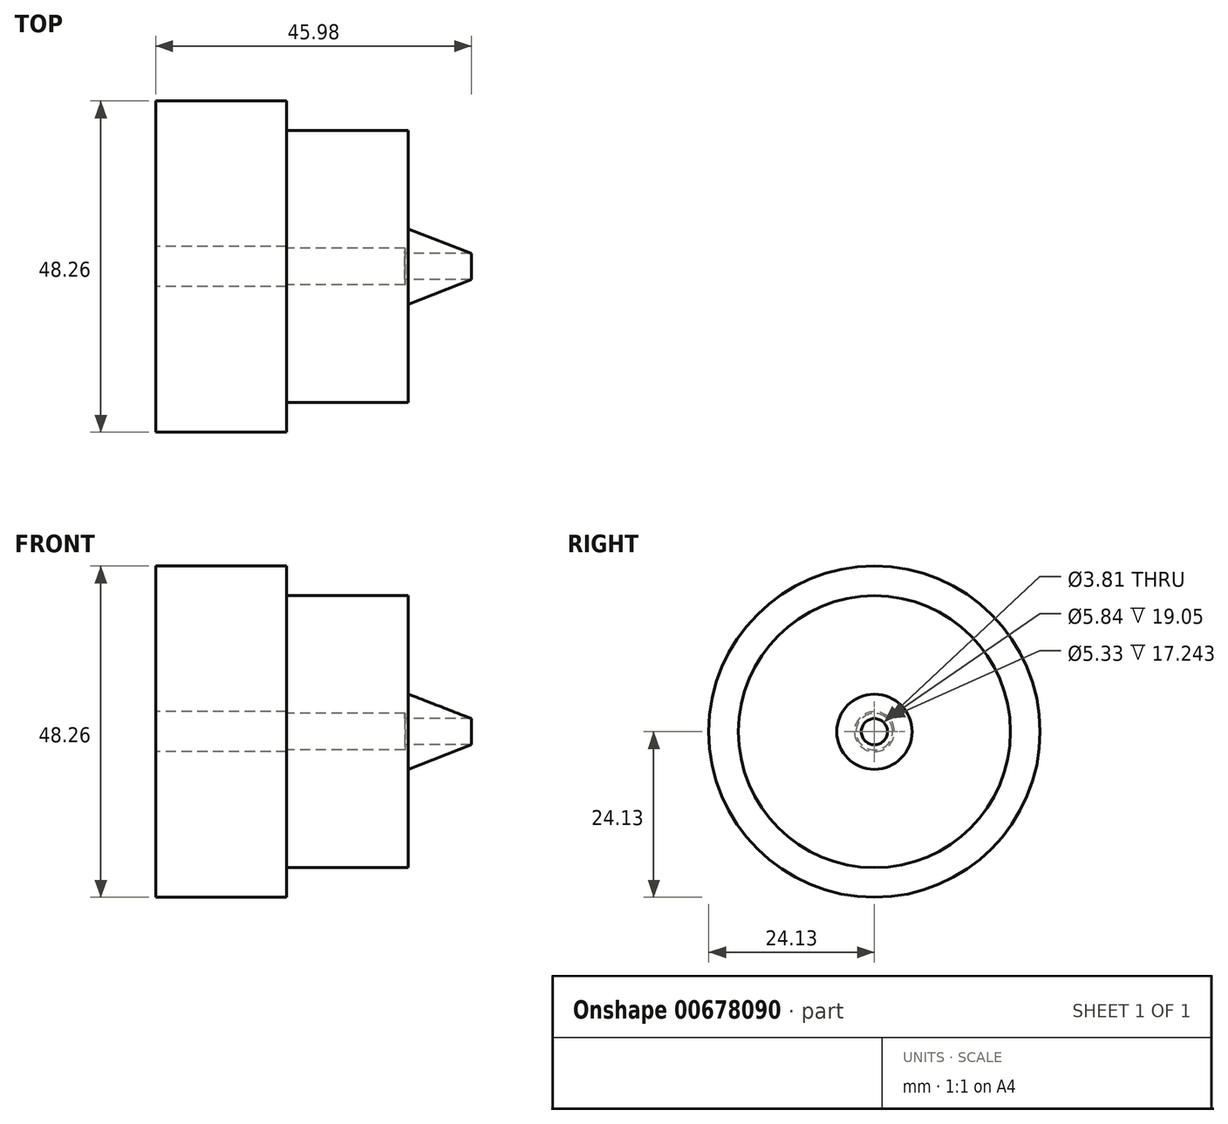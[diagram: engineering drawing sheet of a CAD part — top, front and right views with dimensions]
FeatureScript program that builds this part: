
annotation { "Feature Type Name" : "Feature", "Feature Type Description" : "" }
export const myFeature = defineFeature(function(context is Context, id is Id, definition is map)
    precondition{}
    {
        {
            var Q0;
            Q0=qCreatedBy(makeId("Front.planeOp"),FACE);
            var sketch = newSketch(context, id + "F0", { "sketchPlane" : qUnion([Q0])});
            skLineSegment(sketch, "E0", {"start": v(-45.3, 0) * mm, "end": v(58.06, 0) * mm, "construction": true});
            skLineSegment(sketch, "E1", {"start": v(17.23, 1.9) * mm, "end": v(26.93, 1.9) * mm});
            skLineSegment(sketch, "E2", {"start": v(26.93, 1.9) * mm, "end": v(17.74, 5.48) * mm});
            skLineSegment(sketch, "E3", {"start": v(17.74, 5.48) * mm, "end": v(17.74, 19.81) * mm});
            skLineSegment(sketch, "E4", {"start": v(17.74, 19.81) * mm, "end": v(0, 19.81) * mm});
            skLineSegment(sketch, "E5", {"start": v(0, 19.81) * mm, "end": v(0, 24.13) * mm});
            skLineSegment(sketch, "E6", {"start": v(0, 24.13) * mm, "end": v(-19.05, 24.13) * mm});
            skLineSegment(sketch, "E7", {"start": v(-19.05, 24.13) * mm, "end": v(-19.05, 2.92) * mm});
            skLineSegment(sketch, "E8", {"start": v(-19.05, 2.92) * mm, "end": v(0, 2.92) * mm});
            skLineSegment(sketch, "E9", {"start": v(0, 2.92) * mm, "end": v(0, 2.67) * mm});
            skLineSegment(sketch, "E10", {"start": v(0, 2.67) * mm, "end": v(17.24, 2.67) * mm});
            skLineSegment(sketch, "E11", {"start": v(17.23, 1.9) * mm, "end": v(17.24, 2.67) * mm});
            skSolve(sketch);
        }
        {
            var Q0;
            Q0 = qSketchRegion(id + "F0", true);
            var Q1;
            Q1=sQuery(id+"F0.wireOp",EDGE,"E0");
            revolve(context, id + "F1", {"entities" : qUnion([Q0]), "axis" : qUnion([Q1]), "revolveType" : RevolveType.FULL});
        }
    });
